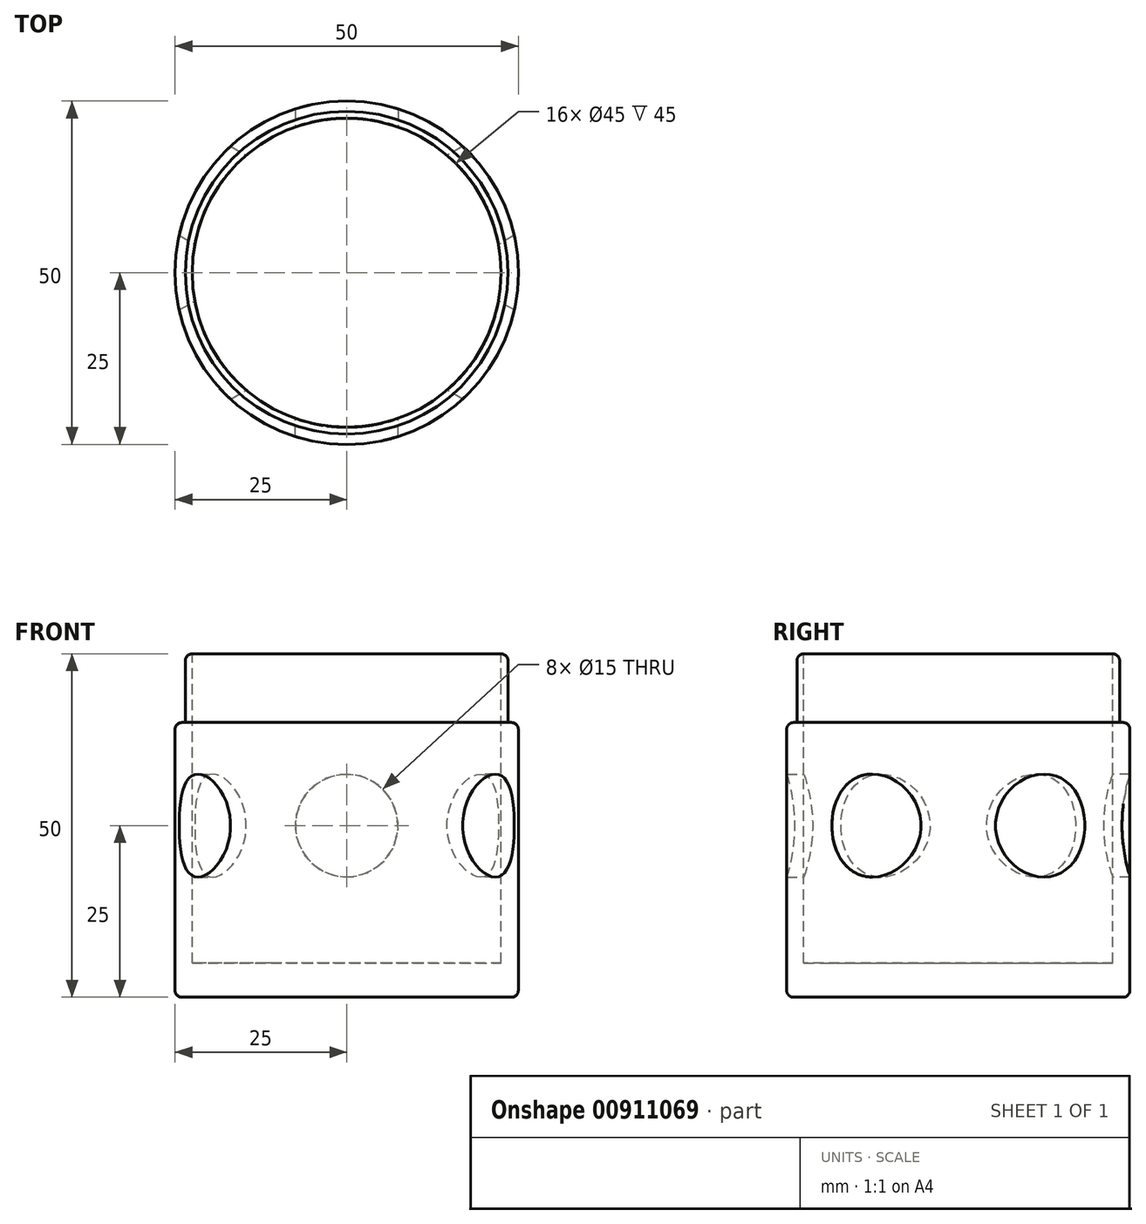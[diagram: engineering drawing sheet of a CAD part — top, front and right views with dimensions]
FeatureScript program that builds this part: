
annotation { "Feature Type Name" : "Feature", "Feature Type Description" : "" }
export const myFeature = defineFeature(function(context is Context, id is Id, definition is map)
    precondition{}
    {
        {
            var Q0;
            Q0=qCreatedBy(makeId("Top.planeOp"),FACE);
            var sketch = newSketch(context, id + "F0", { "sketchPlane" : qUnion([Q0])});
            skCircle(sketch, "E0", {"center": v(0, 0) * mm, "radius": 25 * mm});
            skSolve(sketch);
        }
        {
            var Q0;
            Q0=makeQuery(id+"F0.imprint","IMPRINT",FACE,{"disambiguationData":[TD([[makeQuery(id+"F0.imprint","IMPRINT",EDGE,{"derivedFrom":sQuery(id+"F0.wireOp",EDGE,"E0")}),1.0]])]});
            extrude(context, id + "F1", {"entities" : qUnion([Q0]), "depth" : 40 * mm, "offsetDistance" : 25.4 * mm});
        }
        {
            var Q0;
            Q0=makeQuery(id+"F1.opExtrude","CAP_FACE",FACE,{"disambiguationData":[OSD([sQuery(id+"F0.wireOp",EDGE,"E0")])],"isStart":false});
            var sketch = newSketch(context, id + "F2", { "sketchPlane" : qUnion([Q0])});
            skCircle(sketch, "E1", {"center": v(0, 0) * mm, "radius": 23.5 * mm});
            skSolve(sketch);
        }
        {
            var Q0;
            Q0 = qSketchRegion(id + "F2", true);
            extrude(context, id + "F3", {"entities" : qUnion([Q0]), "operationType" : NewBodyOperationType.ADD, "depth" : 10 * mm, "offsetDistance" : 25.4 * mm});
        }
        {
            var Q0;
            Q0=makeQuery(id+"F3.opExtrude","CAP_FACE",FACE,{"disambiguationData":[OSD([sQuery(id+"F2.wireOp",EDGE,"E1")])],"isStart":false});
            var sketch = newSketch(context, id + "F4", { "sketchPlane" : qUnion([Q0])});
            skCircle(sketch, "E2", {"center": v(0, 0) * mm, "radius": 22.5 * mm});
            skSolve(sketch);
        }
        {
            var Q0;
            Q0=makeQuery(id+"F4.imprint","IMPRINT",FACE,{"disambiguationData":[TD([[makeQuery(id+"F4.imprint","IMPRINT",EDGE,{"derivedFrom":sQuery(id+"F4.wireOp",EDGE,"E2")}),1.0]])]});
            var sketch = newSketch(context, id + "F5", { "sketchPlane" : qUnion([Q0])});
            skSolve(sketch);
        }
        {
            var Q0;
            Q0 = qSketchRegion(id + "F5", true);
            var Q1;
            Q1=makeQuery(id+"F4.imprint","IMPRINT",FACE,{"disambiguationData":[TD([[makeQuery(id+"F4.imprint","IMPRINT",EDGE,{"derivedFrom":sQuery(id+"F4.wireOp",EDGE,"E2")}),1.0]])]});
            extrude(context, id + "F6", {"entities" : qUnion([Q0, Q1]), "operationType" : NewBodyOperationType.REMOVE, "oppositeDirection" : true, "depth" : 45 * mm, "offsetDistance" : 25.4 * mm});
        }
        {
            var Q0;
            Q0=makeQuery(id+"F1.opExtrude","CAP_EDGE",EDGE,{"disambiguationData":[OSD([sQuery(id+"F0.wireOp",EDGE,"E0")])],"isStart":false});
            fillet(context, id + "F7", {"entities" : qUnion([Q0]), "radius" : 1 * mm, "tangentPropagation" : true, "allowEdgeOverflow" : false});
        }
        {
            var Q0;
            Q0=makeQuery(id+"F3.opExtrude","CAP_EDGE",EDGE,{"disambiguationData":[OSD([sQuery(id+"F2.wireOp",EDGE,"E1")])],"isStart":false});
            fillet(context, id + "F8", {"entities" : qUnion([Q0]), "radius" : 1 * mm, "tangentPropagation" : true, "allowEdgeOverflow" : false});
        }
        {
            var Q0;
            Q0=makeQuery(id+"F1.opExtrude","CAP_EDGE",EDGE,{"disambiguationData":[OSD([sQuery(id+"F0.wireOp",EDGE,"E0")])],"isStart":true});
            fillet(context, id + "F9", {"entities" : qUnion([Q0]), "radius" : 1 * mm, "tangentPropagation" : true, "allowEdgeOverflow" : false});
        }
        {
            var Q0;
            Q0=qCreatedBy(makeId("Front.planeOp"),FACE);
            var sketch = newSketch(context, id + "F10", { "sketchPlane" : qUnion([Q0])});
            skCircle(sketch, "E3", {"center": v(0, 25) * mm, "radius": 7.5 * mm});
            skSolve(sketch);
        }
        {
            var Q0;
            Q0 = qSketchRegion(id + "F10", true);
            extrude(context, id + "F11", {"entities" : qUnion([Q0]), "operationType" : NewBodyOperationType.REMOVE, "endBound" : BoundingType.THROUGH_ALL, "oppositeDirection" : true, "depth" : 25.4 * mm, "offsetDistance" : 25.4 * mm});
        }
        {
            var Q0;
            Q0=makeQuery(id+"F1.opExtrude","SWEPT_BODY",BODY,{"disambiguationData":[OSD([sQuery(id+"F0.wireOp",EDGE,"E0")])]});
            var Q1;
            Q1=makeQuery(id+"F1.opExtrude","SWEPT_FACE",FACE,{"disambiguationData":[OSD([sQuery(id+"F0.wireOp",EDGE,"E0")])]});
            circularPattern(context, id + "F12", {"entities" : qUnion([Q0]), "axis" : qUnion([Q1]), "angle" : 360 * degree, "instanceCount" : 6, "equalSpace" : true, "isCentered" : true});
        }
        {
            var Q0;
            Q0=sQuery(id+"F10.wireOp",VERTEX,"E3.center");
            var Q1;
            Q1=makeQuery(id+"F1.opExtrude","SWEPT_BODY",BODY,{"disambiguationData":[OSD([sQuery(id+"F0.wireOp",EDGE,"E0")])]});
            hole(context, id + "F13", {"style" : HoleStyle.SIMPLE, "endStyle" : HoleEndStyle.THROUGH, "oppositeDirection" : true, "holeDiameter" : 15 * mm, "majorDiameter" : 6.35 * mm, "isTappedThrough" : true, "tappedDepth" : 12.7 * mm, "tapClearance" : 3, "locations" : qUnion([Q0]), "scope" : qUnion([Q1])});
        }
        {
            var Q0;
            Q0=makeQuery(id+"F1.opExtrude","SWEPT_BODY",BODY,{"disambiguationData":[OSD([sQuery(id+"F0.wireOp",EDGE,"E0")])]});
            var Q1;
            Q1=makeQuery(id+"F1.opExtrude","SWEPT_FACE",FACE,{"disambiguationData":[OSD([sQuery(id+"F0.wireOp",EDGE,"E0")])]});
            circularPattern(context, id + "F14", {"entities" : qUnion([Q0]), "axis" : qUnion([Q1]), "angle" : 360 * degree, "instanceCount" : 6, "equalSpace" : true});
        }
        {
            var Q0;
            Q0=sQuery(id+"F10.wireOp",VERTEX,"E3.center");
            var Q1;
            Q1=makeQuery(id+"F14.opPattern","COPY",BODY,{"derivedFrom":makeQuery(id+"F1.opExtrude","SWEPT_BODY",BODY,{"disambiguationData":[OSD([sQuery(id+"F0.wireOp",EDGE,"E0")])]}),"instanceName":"1"});
            var Q2;
            Q2=makeQuery(id+"F1.opExtrude","SWEPT_BODY",BODY,{"disambiguationData":[OSD([sQuery(id+"F0.wireOp",EDGE,"E0")])]});
            var Q3;
            Q3=makeQuery(id+"F14.opPattern","COPY",BODY,{"derivedFrom":makeQuery(id+"F1.opExtrude","SWEPT_BODY",BODY,{"disambiguationData":[OSD([sQuery(id+"F0.wireOp",EDGE,"E0")])]}),"instanceName":"2"});
            hole(context, id + "F15", {"style" : HoleStyle.SIMPLE, "endStyle" : HoleEndStyle.THROUGH, "holeDiameter" : 15 * mm, "majorDiameter" : 6.35 * mm, "isTappedThrough" : true, "tappedDepth" : 12.7 * mm, "tapClearance" : 3, "locations" : qUnion([Q0]), "scope" : qUnion([Q1, Q2, Q3])});
        }
    });
